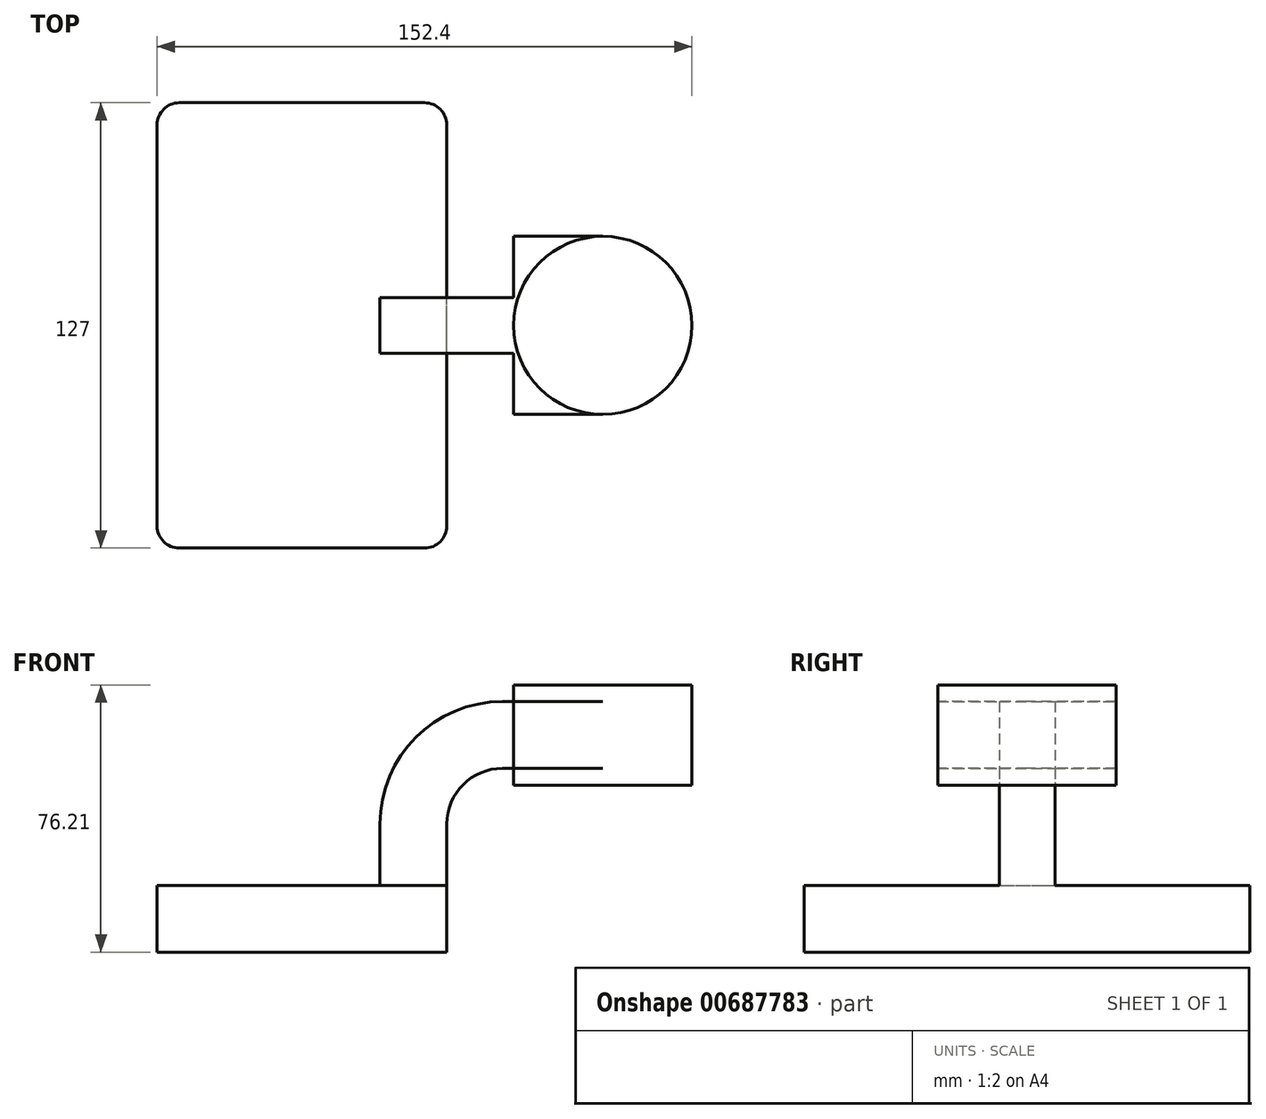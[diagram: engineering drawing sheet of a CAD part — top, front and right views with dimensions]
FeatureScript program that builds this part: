
annotation { "Feature Type Name" : "Feature", "Feature Type Description" : "" }
export const myFeature = defineFeature(function(context is Context, id is Id, definition is map)
    precondition{}
    {
        {
            var Q0;
            Q0=qCreatedBy(makeId("Front.planeOp"),FACE);
            var sketch = newSketch(context, id + "F0", { "sketchPlane" : qUnion([Q0])});
            skLineSegment(sketch, "E0.bottom", {"start": v(41.27, 9.53) * mm, "end": v(-41.28, 9.53) * mm});
            skLineSegment(sketch, "E0.top", {"start": v(41.28, -9.52) * mm, "end": v(-41.27, -9.52) * mm});
            skLineSegment(sketch, "E0.left", {"start": v(41.28, 9.53) * mm, "end": v(41.28, -9.52) * mm});
            skLineSegment(sketch, "E0.right", {"start": v(-41.28, 9.53) * mm, "end": v(-41.27, -9.52) * mm});
            skPoint(sketch, "E0.middle", {"position": v(0, 0) * mm});
            skLineSegment(sketch, "E1.bottom", {"start": v(111.12, 66.68) * mm, "end": v(60.32, 66.68) * mm});
            skLineSegment(sketch, "E1.top", {"start": v(111.13, 38.1) * mm, "end": v(60.33, 38.1) * mm});
            skLineSegment(sketch, "E1.left", {"start": v(111.12, 66.68) * mm, "end": v(111.13, 38.1) * mm});
            skLineSegment(sketch, "E1.right", {"start": v(60.32, 66.68) * mm, "end": v(60.32, 38.1) * mm});
            skPoint(sketch, "E1.middle", {"position": v(85.72, 52.39) * mm});
            skLineSegment(sketch, "E2", {"start": v(41.27, 9.53) * mm, "end": v(41.27, 27) * mm});
            skArc(sketch, "E3", {"start": v(41.27, 27) * mm, "mid": v(45.92, 38.23) * mm, "end": v(57.15, 42.88) * mm});
            skLineSegment(sketch, "E4", {"start": v(57.15, 42.88) * mm, "end": v(85.72, 42.88) * mm});
            skLineSegment(sketch, "E5.0", {"start": v(57.15, 61.93) * mm, "end": v(85.72, 61.93) * mm});
            skArc(sketch, "E5.1", {"start": v(22.23, 27) * mm, "mid": v(32.45, 51.7) * mm, "end": v(57.15, 61.93) * mm});
            skLineSegment(sketch, "E5.2", {"start": v(22.22, 9.53) * mm, "end": v(22.22, 27) * mm});
            skLineSegment(sketch, "E6", {"start": v(85.72, 38.1) * mm, "end": v(85.72, 66.68) * mm});
            skFitSpline(sketch, "E7", {"points": [v(-41.28, 9.53) * mm, v(57.15, 61.93) * mm], "startDerivative": vector(0, 54.22) * mm, "endDerivative": vector(171.45, 0) * mm});
            skSolve(sketch);
        }
        {
            var Q0;
            Q0=makeQuery(id+"F0.imprint","IMPRINT",FACE,{"disambiguationData":[TD([[makeQuery(id+"F0.imprint","IMPRINT",EDGE,{"derivedFrom":sQuery(id+"F0.wireOp",EDGE,"E0.top")}),-1.0]])]});
            extrude(context, id + "F1", {"entities" : qUnion([Q0]), "endBound" : BoundingType.SYMMETRIC, "depth" : 127 * mm, "offsetDistance" : 25.4 * mm});
        }
        {
            var Q0;
            {var subQ0=sQuery(id+"F0.wireOp",EDGE,"E3");Q0=makeQuery(id+"F0.imprint","IMPRINT",FACE,{"disambiguationData":[TD([[makeQuery(id+"F0.imprint","IMPRINT",EDGE,{"derivedFrom":subQ0}),1.0]])]});}
            var Q1;
            {var subQ0=sQuery(id+"F0.wireOp",EDGE,"E5.0");var subQ1=sQuery(id+"F0.wireOp",EDGE,"E1.right");var subQ2=makeQuery(id+"F0.imprint","INTERSECT",VERTEX,{"derivedFrom":[subQ1,subQ0]});Q1=makeQuery(id+"F0.imprint","IMPRINT",FACE,{"disambiguationData":[TD([[makeQuery(id+"F0.imprint","IMPRINT",EDGE,{"disambiguationData":[TD([[subQ2,-1.0]])],"derivedFrom":subQ1}),1.0]])]});}
            extrude(context, id + "F2", {"entities" : qUnion([Q0, Q1]), "endBound" : BoundingType.SYMMETRIC, "depth" : 50.8 * mm, "offsetDistance" : 25.4 * mm});
        }
        {
            var Q0;
            Q0=makeQuery(id+"F0.imprint","IMPRINT",FACE,{"disambiguationData":[TD([[makeQuery(id+"F0.imprint","IMPRINT",EDGE,{"derivedFrom":sQuery(id+"F0.wireOp",EDGE,"E5.1")}),1.0]])]});
            extrude(context, id + "F3", {"entities" : qUnion([Q0]), "operationType" : NewBodyOperationType.ADD, "endBound" : BoundingType.SYMMETRIC, "depth" : 15.88 * mm, "offsetDistance" : 25.4 * mm});
        }
        {
            var Q0;
            {var subQ4=sQuery(id+"F0.wireOp",EDGE,"E1.left");Q0=makeQuery(id+"F0.imprint","IMPRINT",FACE,{"disambiguationData":[TD([[makeQuery(id+"F0.imprint","IMPRINT",EDGE,{"derivedFrom":subQ4}),-1.0]])]});}
            var Q1;
            Q1=sQuery(id+"F0.wireOp",EDGE,"E6");
            revolve(context, id + "F4", {"operationType" : NewBodyOperationType.ADD, "entities" : qUnion([Q0]), "axis" : qUnion([Q1]), "revolveType" : RevolveType.FULL});
        }
        {
            var Q0;
            Q0=makeQuery(id+"F1.opExtrude","CAP_EDGE",EDGE,{"disambiguationData":[OSD([sQuery(id+"F0.wireOp",EDGE,"E0.left")])],"isStart":false});
            var Q1;
            Q1=makeQuery(id+"F1.opExtrude","CAP_EDGE",EDGE,{"disambiguationData":[OSD([sQuery(id+"F0.wireOp",EDGE,"E0.right")])],"isStart":false});
            var Q2;
            Q2=makeQuery(id+"F1.opExtrude","CAP_EDGE",EDGE,{"disambiguationData":[OSD([sQuery(id+"F0.wireOp",EDGE,"E0.left")])],"isStart":true});
            var Q3;
            Q3=makeQuery(id+"F1.opExtrude","CAP_EDGE",EDGE,{"disambiguationData":[OSD([sQuery(id+"F0.wireOp",EDGE,"E0.right")])],"isStart":true});
            fillet(context, id + "F5", {"entities" : qUnion([Q0, Q1, Q2, Q3]), "radius" : 6.35 * mm, "tangentPropagation" : true, "allowEdgeOverflow" : false});
        }
    });
